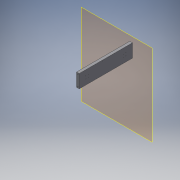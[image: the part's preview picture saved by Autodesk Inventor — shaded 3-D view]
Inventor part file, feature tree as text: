
AUTODESK INVENTOR PART (.ipt)
format: ipt  version: 2019 (Build 230136000, 136)  size: 208,896 bytes
history: native  units: in
note: dims shown in document units (in); Inventor stores cm internally (conversion verified against a paired STEP export)
features: reference x14, sketch x7, extrude x7, other x7, thread x4, plane x2, projected_geometry x1, helix x1
ambient origin geometry x8: Origin, YZ Plane, XZ Plane, XY Plane, X Axis, Y Axis, Z Axis, Center Point
bodies: Solid1 (feature_tree)
feature tree (43):
  plane  "Work Plane1"
  sketch  "Sketch1"  dims[d0=0.7874in d1=1.0in d2=0.0in]
  plane  "Work Plane2"
  extrude  "Extrusion1"  Depth=0.7874in TaperAngle=0.0deg
  extrude  "Extrusion2"  Depth=0.1181in
  extrude  "Extrusion3"  Depth=0.1181in
  extrude  "Extrusion4"  Depth=0.1181in
  extrude  "Extrusion5"  Depth=0.1181in
  extrude  "Extrusion6"  Depth=0.315in
  thread  "Thread1"  [1 undecoded]
  thread  "Thread2"  [1 undecoded]
  extrude  "Extrusion7"  Depth=0.7874in
  thread  "Thread3"  [1 undecoded]
  thread  "Thread4"  [1 undecoded]
  reference  "Reference1"
  sketch  "Sketch2"  dims[d3=0.1181in d4=0.1181in]
  reference  "Reference2"
  reference  "Reference3"
  reference  "Reference4"
  reference  "Reference5"
  reference  "Reference6"
  reference  "Reference7"
  reference  "Reference8"
  reference  "Reference9"
  sketch  "Sketch3"  dims[d5=0.1181in d6=0.1181in]
  projected_geometry  "Projected Loop1"
  sketch  "Sketch4"  dims[d7=0.1181in d8=0.1181in]
  reference  "Reference10"
  reference  "Reference11"
  sketch  "Sketch5"  dims[d9=0.1181in d10=0.1181in]
  sketch  "Sketch6"  dims[d11=1.0in d12=0.0in d13=0.315in d14=0.315in d15=0.315in]
  reference  "Reference12"
  reference  "Reference13"
  sketch  "Sketch7"  dims[d16=0.315in d17=0.315in d18=0.315in d19=0.315in d20=0.315in d21=0.1969in d22=0.0in d23=0.1575in d24=0.1575in d25=0.1969in d26=0.0in d27=0.3937in d28=0.3937in d29=0.2362in d30=0.0in d31=0.1969in d32=0.1969in d33=0.7874in d34=0.0in d35=1.0in d36=0.0in d37=1.0in d38=0.0in d39=0.1969in d40=0.1969in d41=0.7874in d42=0.0in d43=1.0in d44=0.0in d45=1.0in d46=0.0in]
  reference  "Reference14"
  other  "<userpath>\Documents\CAD Files\Helix DLP\Helix DLP Z Stage.iam"
  helix  "Helix DLP Z Stage.iam"  [1 undecoded]
  other  "Z stage_side:1"
  other  "MGN12H, LINEAR GUIDE BLOCK:1"
  other  "MGN12H, LINEAR GUIDE BLOCK:2"
  other  "Z Leadcrew Nut Holder:1"
  other  "Z stage_side:2"
  other  "Assembly1"
note: 5 required parameter values undecoded (feature->parameter linkage not recoverable at this tier; creation-order binding heuristic only, values carry confidence <= 0.55)
